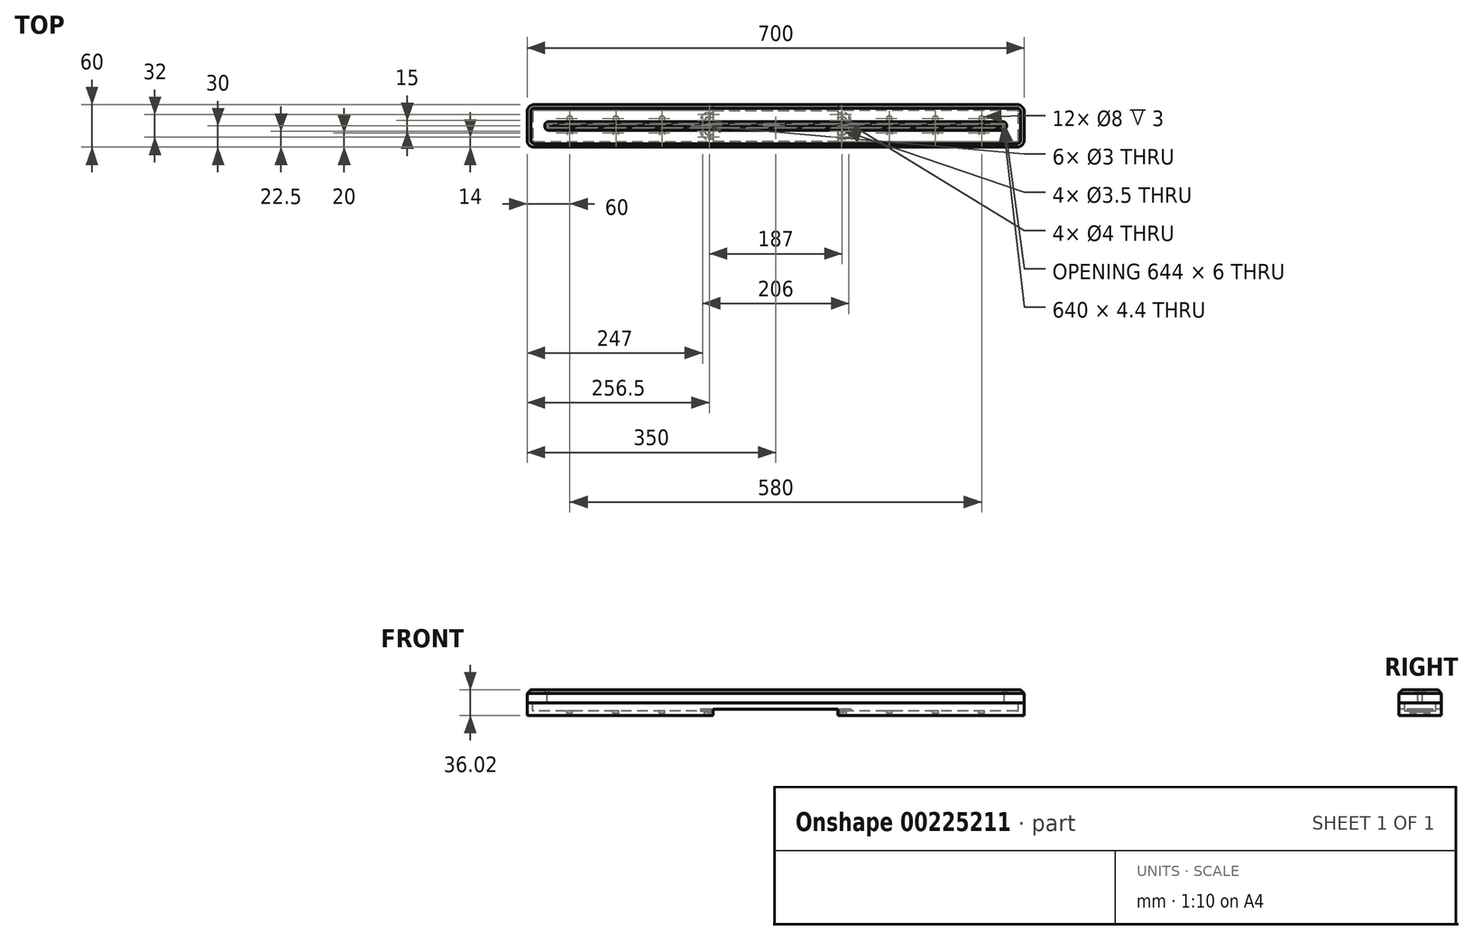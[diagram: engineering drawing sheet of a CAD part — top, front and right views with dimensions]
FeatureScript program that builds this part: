
annotation { "Feature Type Name" : "Feature", "Feature Type Description" : "" }
export const myFeature = defineFeature(function(context is Context, id is Id, definition is map)
    precondition{}
    {
        {
            var Q0;
            Q0=qCreatedBy(makeId("Top.planeOp"),FACE);
            var sketch = newSketch(context, id + "F0", { "sketchPlane" : qUnion([Q0])});
            skLineSegment(sketch, "E0.bottom", {"start": v(350, 30) * mm, "end": v(-350, 30) * mm});
            skLineSegment(sketch, "E0.top", {"start": v(350, -30) * mm, "end": v(-350, -30) * mm});
            skLineSegment(sketch, "E0.left", {"start": v(350, 30) * mm, "end": v(350, -30) * mm});
            skLineSegment(sketch, "E0.right", {"start": v(-350, 30) * mm, "end": v(-350, -30) * mm});
            skPoint(sketch, "E0.middle", {"position": v(0, 0) * mm});
            skSolve(sketch);
        }
        {
            var Q0;
            Q0=makeQuery(id+"F0.imprint","IMPRINT",FACE,{"disambiguationData":[TD([[makeQuery(id+"F0.imprint","IMPRINT",EDGE,{"derivedFrom":sQuery(id+"F0.wireOp",EDGE,"E0.bottom")}),1.0]])]});
            extrude(context, id + "F1", {"entities" : qUnion([Q0]), "depth" : 18 * mm});
        }
        {
            var Q0;
            Q0=makeQuery(id+"F1.opExtrude","CAP_FACE",FACE,{"disambiguationData":[OSD([sQuery(id+"F0.wireOp",EDGE,"E0.bottom"),sQuery(id+"F0.wireOp",EDGE,"E0.top"),sQuery(id+"F0.wireOp",EDGE,"E0.left"),sQuery(id+"F0.wireOp",EDGE,"E0.right")])],"isStart":false});
            extrude(context, id + "F2", {"entities" : qUnion([Q0]), "depth" : 18 * mm});
        }
        {
            var Q0;
            Q0=makeQuery(id+"F1.opExtrude","SWEPT_EDGE",EDGE,{"disambiguationData":[OSD([sQuery(id+"F0.wireOp",EDGE,"E0.top"),sQuery(id+"F0.wireOp",EDGE,"E0.right")])]});
            var Q1;
            Q1=makeQuery(id+"F2.opExtrude","SWEPT_EDGE",EDGE,{"disambiguationData":[OSD([sQuery(id+"F0.wireOp",EDGE,"E0.top"),sQuery(id+"F0.wireOp",EDGE,"E0.right")])]});
            var Q2;
            Q2=makeQuery(id+"F2.opExtrude","SWEPT_EDGE",EDGE,{"disambiguationData":[OSD([sQuery(id+"F0.wireOp",EDGE,"E0.top"),sQuery(id+"F0.wireOp",EDGE,"E0.left")])]});
            var Q3;
            Q3=makeQuery(id+"F1.opExtrude","SWEPT_EDGE",EDGE,{"disambiguationData":[OSD([sQuery(id+"F0.wireOp",EDGE,"E0.top"),sQuery(id+"F0.wireOp",EDGE,"E0.left")])]});
            var Q4;
            Q4=makeQuery(id+"F2.opExtrude","SWEPT_EDGE",EDGE,{"disambiguationData":[OSD([sQuery(id+"F0.wireOp",EDGE,"E0.bottom"),sQuery(id+"F0.wireOp",EDGE,"E0.left")])]});
            var Q5;
            Q5=makeQuery(id+"F1.opExtrude","SWEPT_EDGE",EDGE,{"disambiguationData":[OSD([sQuery(id+"F0.wireOp",EDGE,"E0.bottom"),sQuery(id+"F0.wireOp",EDGE,"E0.left")])]});
            var Q6;
            Q6=makeQuery(id+"F2.opExtrude","SWEPT_EDGE",EDGE,{"disambiguationData":[OSD([sQuery(id+"F0.wireOp",EDGE,"E0.bottom"),sQuery(id+"F0.wireOp",EDGE,"E0.right")])]});
            var Q7;
            Q7=makeQuery(id+"F1.opExtrude","SWEPT_EDGE",EDGE,{"disambiguationData":[OSD([sQuery(id+"F0.wireOp",EDGE,"E0.bottom"),sQuery(id+"F0.wireOp",EDGE,"E0.right")])]});
            fillet(context, id + "F3", {"entities" : qUnion([Q0, Q1, Q2, Q3, Q4, Q5, Q6, Q7]), "radius" : 10 * mm, "tangentPropagation" : true, "allowEdgeOverflow" : false});
        }
        {
            var Q0;
            Q0=makeQuery(id+"F2.opExtrude","CAP_EDGE",EDGE,{"disambiguationData":[OSD([sQuery(id+"F0.wireOp",EDGE,"E0.bottom")])],"isStart":false});
            chamfer(context, id + "F4", {"entities" : qUnion([Q0]), "width" : 5 * mm, "tangentPropagation" : true});
        }
        {
            var Q0;
            Q0=makeQuery(id+"F2.opExtrude","CAP_FACE",FACE,{"disambiguationData":[OSD([sQuery(id+"F0.wireOp",EDGE,"E0.bottom"),sQuery(id+"F0.wireOp",EDGE,"E0.top"),sQuery(id+"F0.wireOp",EDGE,"E0.left"),sQuery(id+"F0.wireOp",EDGE,"E0.right")])],"isStart":false});
            var sketch = newSketch(context, id + "F5", { "sketchPlane" : qUnion([Q0])});
            skLineSegment(sketch, "E1.bottom", {"start": v(-325, 6) * mm, "end": v(325, 6) * mm});
            skLineSegment(sketch, "E1.top", {"start": v(-325, -6) * mm, "end": v(325, -6) * mm});
            skLineSegment(sketch, "E1.left", {"start": v(-325, 6) * mm, "end": v(-325, -6) * mm});
            skLineSegment(sketch, "E1.right", {"start": v(325, 6) * mm, "end": v(325, -6) * mm});
            skPoint(sketch, "E1.middle", {"position": v(0, 0) * mm});
            skSolve(sketch);
        }
        {
            var Q0;
            Q0=makeQuery(id+"F5.imprint","IMPRINT",FACE,{"disambiguationData":[TD([[makeQuery(id+"F5.imprint","IMPRINT",EDGE,{"derivedFrom":sQuery(id+"F5.wireOp",EDGE,"E1.bottom")}),-1.0]])]});
            extrude(context, id + "F6", {"entities" : qUnion([Q0]), "operationType" : NewBodyOperationType.REMOVE, "oppositeDirection" : true, "depth" : 4.4 * mm});
        }
        {
            var Q0;
            Q0=makeQuery(id+"F6.boolean.opBoolean","COPY",EDGE,{"derivedFrom":makeQuery(id+"F6.opExtrude","SWEPT_EDGE",EDGE,{"disambiguationData":[OSD([sQuery(id+"F5.wireOp",EDGE,"E1.bottom"),sQuery(id+"F5.wireOp",EDGE,"E1.left")])]})});
            var Q1;
            Q1=makeQuery(id+"F6.boolean.opBoolean","COPY",EDGE,{"derivedFrom":makeQuery(id+"F6.opExtrude","SWEPT_EDGE",EDGE,{"disambiguationData":[OSD([sQuery(id+"F5.wireOp",EDGE,"E1.top"),sQuery(id+"F5.wireOp",EDGE,"E1.left")])]})});
            var Q2;
            Q2=makeQuery(id+"F6.boolean.opBoolean","COPY",EDGE,{"derivedFrom":makeQuery(id+"F6.opExtrude","SWEPT_EDGE",EDGE,{"disambiguationData":[OSD([sQuery(id+"F5.wireOp",EDGE,"E1.bottom"),sQuery(id+"F5.wireOp",EDGE,"E1.right")])]})});
            var Q3;
            Q3=makeQuery(id+"F6.boolean.opBoolean","COPY",EDGE,{"derivedFrom":makeQuery(id+"F6.opExtrude","SWEPT_EDGE",EDGE,{"disambiguationData":[OSD([sQuery(id+"F5.wireOp",EDGE,"E1.top"),sQuery(id+"F5.wireOp",EDGE,"E1.right")])]})});
            fillet(context, id + "F7", {"entities" : qUnion([Q0, Q1, Q2, Q3]), "radius" : 5 * mm, "tangentPropagation" : true, "allowEdgeOverflow" : false});
        }
        {
            var Q0;
            Q0=makeQuery(id+"F6.boolean.opBoolean","COPY",FACE,{"derivedFrom":makeQuery(id+"F6.opExtrude","CAP_FACE",FACE,{"disambiguationData":[OSD([sQuery(id+"F5.wireOp",EDGE,"E1.bottom"),sQuery(id+"F5.wireOp",EDGE,"E1.top"),sQuery(id+"F5.wireOp",EDGE,"E1.left"),sQuery(id+"F5.wireOp",EDGE,"E1.right")])],"isStart":false})});
            var sketch = newSketch(context, id + "F8", { "sketchPlane" : qUnion([Q0])});
            skArc(sketch, "E2.0", {"start": v(-320, 3) * mm, "mid": v(-321.41, 2.41) * mm, "end": v(-322, 1) * mm});
            skLineSegment(sketch, "E2.1", {"start": v(320, 3) * mm, "end": v(-320, 3) * mm});
            skLineSegment(sketch, "E2.2", {"start": v(-322, 1) * mm, "end": v(-322, -1) * mm});
            skArc(sketch, "E2.3", {"start": v(322, 1) * mm, "mid": v(321.41, 2.41) * mm, "end": v(320, 3) * mm});
            skArc(sketch, "E2.4", {"start": v(-322, -1) * mm, "mid": v(-321.41, -2.41) * mm, "end": v(-320, -3) * mm});
            skLineSegment(sketch, "E2.5", {"start": v(-320, -3) * mm, "end": v(320, -3) * mm});
            skArc(sketch, "E2.6", {"start": v(320, -3) * mm, "mid": v(321.41, -2.41) * mm, "end": v(322, -1) * mm});
            skLineSegment(sketch, "E2.7", {"start": v(322, -1) * mm, "end": v(322, 1) * mm});
            skSolve(sketch);
        }
        {
            var Q0;
            Q0=makeQuery(id+"F8.imprint","IMPRINT",FACE,{"disambiguationData":[TD([[makeQuery(id+"F8.imprint","IMPRINT",EDGE,{"derivedFrom":sQuery(id+"F8.wireOp",EDGE,"E2.0")}),1.0]])]});
            extrude(context, id + "F9", {"entities" : qUnion([Q0]), "operationType" : NewBodyOperationType.REMOVE, "oppositeDirection" : true, "depth" : 25 * mm});
        }
        {
            var Q0;
            Q0=makeQuery(id+"F1.opExtrude","CAP_FACE",FACE,{"disambiguationData":[OSD([sQuery(id+"F0.wireOp",EDGE,"E0.bottom"),sQuery(id+"F0.wireOp",EDGE,"E0.top"),sQuery(id+"F0.wireOp",EDGE,"E0.left"),sQuery(id+"F0.wireOp",EDGE,"E0.right")])],"isStart":false});
            var sketch = newSketch(context, id + "F10", { "sketchPlane" : qUnion([Q0])});
            skArc(sketch, "E3.0", {"start": v(-342, -20) * mm, "mid": v(-341.41, -21.41) * mm, "end": v(-340, -22) * mm});
            skLineSegment(sketch, "E3.1", {"start": v(-342, 20) * mm, "end": v(-342, -20) * mm});
            skLineSegment(sketch, "E3.2", {"start": v(-340, -22) * mm, "end": v(340, -22) * mm});
            skArc(sketch, "E3.3", {"start": v(-340, 22) * mm, "mid": v(-341.41, 21.41) * mm, "end": v(-342, 20) * mm});
            skArc(sketch, "E3.4", {"start": v(340, -22) * mm, "mid": v(341.41, -21.41) * mm, "end": v(342, -20) * mm});
            skLineSegment(sketch, "E3.5", {"start": v(342, -20) * mm, "end": v(342, 20) * mm});
            skArc(sketch, "E3.6", {"start": v(342, 20) * mm, "mid": v(341.41, 21.41) * mm, "end": v(340, 22) * mm});
            skLineSegment(sketch, "E3.7", {"start": v(340, 22) * mm, "end": v(-340, 22) * mm});
            skSolve(sketch);
        }
        {
            var Q0;
            Q0 = qSketchRegion(id + "F10", true);
            extrude(context, id + "F11", {"entities" : qUnion([Q0]), "operationType" : NewBodyOperationType.REMOVE, "oppositeDirection" : true, "depth" : (18 - 6) * mm});
        }
        {
            var Q0;
            Q0=makeQuery(id+"F11.boolean.opBoolean","COPY",FACE,{"derivedFrom":makeQuery(id+"F11.opExtrude","CAP_FACE",FACE,{"disambiguationData":[OSD([sQuery(id+"F10.wireOp",EDGE,"E3.0"),sQuery(id+"F10.wireOp",EDGE,"E3.1"),sQuery(id+"F10.wireOp",EDGE,"E3.2"),sQuery(id+"F10.wireOp",EDGE,"E3.3"),sQuery(id+"F10.wireOp",EDGE,"E3.4"),sQuery(id+"F10.wireOp",EDGE,"E3.5"),sQuery(id+"F10.wireOp",EDGE,"E3.6"),sQuery(id+"F10.wireOp",EDGE,"E3.7")])],"isStart":false})});
            var sketch = newSketch(context, id + "F12", { "sketchPlane" : qUnion([Q0])});
            skLineSegment(sketch, "E4.bottom", {"start": v(-100, 12.5) * mm, "end": v(100, 12.5) * mm});
            skLineSegment(sketch, "E4.top", {"start": v(-100, -12.5) * mm, "end": v(100, -12.5) * mm});
            skLineSegment(sketch, "E4.left", {"start": v(-100, 12.5) * mm, "end": v(-100, -12.5) * mm});
            skLineSegment(sketch, "E4.right", {"start": v(100, 12.5) * mm, "end": v(100, -12.5) * mm});
            skPoint(sketch, "E4.middle", {"position": v(0, 0) * mm});
            skSolve(sketch);
        }
        {
            var Q0;
            Q0=makeQuery(id+"F12.imprint","IMPRINT",FACE,{"disambiguationData":[TD([[makeQuery(id+"F12.imprint","IMPRINT",EDGE,{"derivedFrom":sQuery(id+"F12.wireOp",EDGE,"E4.bottom")}),-1.0]])]});
            extrude(context, id + "F13", {"entities" : qUnion([Q0]), "operationType" : NewBodyOperationType.REMOVE, "oppositeDirection" : true, "depth" : 25 * mm});
        }
        {
            var Q0;
            Q0=makeQuery(id+"F13.boolean.opBoolean","COPY",EDGE,{"derivedFrom":makeQuery(id+"F13.opExtrude","SWEPT_EDGE",EDGE,{"disambiguationData":[OSD([sQuery(id+"F12.wireOp",EDGE,"E4.bottom"),sQuery(id+"F12.wireOp",EDGE,"E4.right")])]})});
            var Q1;
            Q1=makeQuery(id+"F13.boolean.opBoolean","COPY",EDGE,{"derivedFrom":makeQuery(id+"F13.opExtrude","SWEPT_EDGE",EDGE,{"disambiguationData":[OSD([sQuery(id+"F12.wireOp",EDGE,"E4.top"),sQuery(id+"F12.wireOp",EDGE,"E4.right")])]})});
            var Q2;
            Q2=makeQuery(id+"F13.boolean.opBoolean","COPY",EDGE,{"derivedFrom":makeQuery(id+"F13.opExtrude","SWEPT_EDGE",EDGE,{"disambiguationData":[OSD([sQuery(id+"F12.wireOp",EDGE,"E4.top"),sQuery(id+"F12.wireOp",EDGE,"E4.left")])]})});
            var Q3;
            Q3=makeQuery(id+"F13.boolean.opBoolean","COPY",EDGE,{"derivedFrom":makeQuery(id+"F13.opExtrude","SWEPT_EDGE",EDGE,{"disambiguationData":[OSD([sQuery(id+"F12.wireOp",EDGE,"E4.bottom"),sQuery(id+"F12.wireOp",EDGE,"E4.left")])]})});
            fillet(context, id + "F14", {"entities" : qUnion([Q0, Q1, Q2, Q3]), "radius" : 5 * mm, "tangentPropagation" : true, "allowEdgeOverflow" : false});
        }
        {
            var Q0;
            Q0=makeQuery(id+"F11.boolean.opBoolean","COPY",FACE,{"derivedFrom":makeQuery(id+"F11.opExtrude","CAP_FACE",FACE,{"disambiguationData":[OSD([sQuery(id+"F10.wireOp",EDGE,"E3.0"),sQuery(id+"F10.wireOp",EDGE,"E3.1"),sQuery(id+"F10.wireOp",EDGE,"E3.2"),sQuery(id+"F10.wireOp",EDGE,"E3.3"),sQuery(id+"F10.wireOp",EDGE,"E3.4"),sQuery(id+"F10.wireOp",EDGE,"E3.5"),sQuery(id+"F10.wireOp",EDGE,"E3.6"),sQuery(id+"F10.wireOp",EDGE,"E3.7")])],"isStart":false})});
            var sketch = newSketch(context, id + "F15", { "sketchPlane" : qUnion([Q0])});
            skCircle(sketch, "E5", {"center": v(-225, -10) * mm, "radius": 4 * mm});
            skCircle(sketch, "E6", {"center": v(-225, 10) * mm, "radius": 4 * mm});
            skCircle(sketch, "E7", {"center": v(-160, 10) * mm, "radius": 4 * mm});
            skCircle(sketch, "E8", {"center": v(-160, -10) * mm, "radius": 4 * mm});
            skCircle(sketch, "E9", {"center": v(-290, 10) * mm, "radius": 4 * mm});
            skCircle(sketch, "E10", {"center": v(-290, -10) * mm, "radius": 4 * mm});
            skCircle(sketch, "E11.MirrorC", {"center": v(290, -10) * mm, "radius": 4 * mm});
            skCircle(sketch, "E12.MirrorC", {"center": v(160, 10) * mm, "radius": 4 * mm});
            skCircle(sketch, "E13.MirrorC", {"center": v(225, 10) * mm, "radius": 4 * mm});
            skCircle(sketch, "E14.MirrorC", {"center": v(225, -10) * mm, "radius": 4 * mm});
            skCircle(sketch, "E15.MirrorC", {"center": v(290, 10) * mm, "radius": 4 * mm});
            skCircle(sketch, "E16.MirrorC", {"center": v(160, -10) * mm, "radius": 4 * mm});
            skSolve(sketch);
        }
        {
            var Q0;
            Q0 = qSketchRegion(id + "F15", true);
            extrude(context, id + "F16", {"entities" : qUnion([Q0]), "operationType" : NewBodyOperationType.REMOVE, "oppositeDirection" : true, "depth" : 3 * mm});
        }
        {
            var Q0;
            Q0=makeQuery(id+"F6.boolean.opBoolean","COPY",FACE,{"derivedFrom":makeQuery(id+"F6.opExtrude","CAP_FACE",FACE,{"disambiguationData":[OSD([sQuery(id+"F5.wireOp",EDGE,"E1.bottom"),sQuery(id+"F5.wireOp",EDGE,"E1.top"),sQuery(id+"F5.wireOp",EDGE,"E1.left"),sQuery(id+"F5.wireOp",EDGE,"E1.right")])],"isStart":false})});
            var sketch = newSketch(context, id + "F17", { "sketchPlane" : qUnion([Q0])});
            skArc(sketch, "E17.0", {"start": v(-320, 6) * mm, "mid": v(-323.54, 4.54) * mm, "end": v(-325, 1) * mm});
            skLineSegment(sketch, "E17.1", {"start": v(320, 6) * mm, "end": v(-320, 6) * mm});
            skLineSegment(sketch, "E17.2", {"start": v(-325, 1) * mm, "end": v(-325, -1) * mm});
            skArc(sketch, "E17.3", {"start": v(325, 1) * mm, "mid": v(323.54, 4.54) * mm, "end": v(320, 6) * mm});
            skArc(sketch, "E17.4", {"start": v(-325, -1) * mm, "mid": v(-323.54, -4.54) * mm, "end": v(-320, -6) * mm});
            skLineSegment(sketch, "E17.5", {"start": v(-320, -6) * mm, "end": v(320, -6) * mm});
            skArc(sketch, "E17.6", {"start": v(320, -6) * mm, "mid": v(323.54, -4.54) * mm, "end": v(325, -1) * mm});
            skLineSegment(sketch, "E17.7", {"start": v(325, -1) * mm, "end": v(325, 1) * mm});
            skLineSegment(sketch, "E18.bottom", {"start": v(-320, -2.2) * mm, "end": v(320, -2.2) * mm});
            skLineSegment(sketch, "E18.top", {"start": v(-320, 2.2) * mm, "end": v(320, 2.2) * mm});
            skLineSegment(sketch, "E18.left", {"start": v(-320, -2.2) * mm, "end": v(-320, 2.2) * mm});
            skLineSegment(sketch, "E18.right", {"start": v(320, -2.2) * mm, "end": v(320, 2.2) * mm});
            skPoint(sketch, "E18.middle", {"position": v(0, 0) * mm});
            skSolve(sketch);
        }
        {
            var Q0;
            Q0 = qSketchRegion(id + "F17", true);
            extrude(context, id + "F18", {"entities" : qUnion([Q0]), "depth" : 4.42 * mm});
        }
        {
            var Q0;
            Q0=makeQuery(id+"F11.boolean.opBoolean","COPY",FACE,{"derivedFrom":makeQuery(id+"F11.opExtrude","CAP_FACE",FACE,{"disambiguationData":[OSD([sQuery(id+"F10.wireOp",EDGE,"E3.0"),sQuery(id+"F10.wireOp",EDGE,"E3.1"),sQuery(id+"F10.wireOp",EDGE,"E3.2"),sQuery(id+"F10.wireOp",EDGE,"E3.3"),sQuery(id+"F10.wireOp",EDGE,"E3.4"),sQuery(id+"F10.wireOp",EDGE,"E3.5"),sQuery(id+"F10.wireOp",EDGE,"E3.6"),sQuery(id+"F10.wireOp",EDGE,"E3.7")])],"isStart":false})});
            var sketch = newSketch(context, id + "F19", { "sketchPlane" : qUnion([Q0])});
            skArc(sketch, "E19.0", {"start": v(-106, 7.5) * mm, "mid": v(-102.78, 15.28) * mm, "end": v(-95, 18.5) * mm});
            skLineSegment(sketch, "E19.1", {"start": v(-106, 7.5) * mm, "end": v(-106, -7.5) * mm});
            skLineSegment(sketch, "E19.2", {"start": v(-95, 18.5) * mm, "end": v(95, 18.5) * mm});
            skArc(sketch, "E19.3", {"start": v(-95, -18.5) * mm, "mid": v(-102.78, -15.28) * mm, "end": v(-106, -7.5) * mm});
            skArc(sketch, "E19.4", {"start": v(95, 18.5) * mm, "mid": v(102.78, 15.28) * mm, "end": v(106, 7.5) * mm});
            skLineSegment(sketch, "E19.5", {"start": v(106, 7.5) * mm, "end": v(106, -7.5) * mm});
            skArc(sketch, "E19.6", {"start": v(106, -7.5) * mm, "mid": v(102.78, -15.28) * mm, "end": v(95, -18.5) * mm});
            skLineSegment(sketch, "E19.7", {"start": v(-95, -18.5) * mm, "end": v(95, -18.5) * mm});
            skLineSegment(sketch, "E20.2", {"start": v(-86, 10.5) * mm, "end": v(86, 10.5) * mm});
            skLineSegment(sketch, "E20.7", {"start": v(-86, -10.5) * mm, "end": v(86, -10.5) * mm});
            skLineSegment(sketch, "E21", {"start": v(-88, 8.5) * mm, "end": v(-88, -8.5) * mm});
            skLineSegment(sketch, "E22", {"start": v(88, 8.5) * mm, "end": v(88, -8.5) * mm});
            skCircle(sketch, "E23", {"center": v(-103, 0) * mm, "radius": 1.5 * mm});
            skPoint(sketch, "E23.centerSnap0", {"position": v(-106, 0) * mm});
            skCircle(sketch, "E24", {"center": v(-93, 16) * mm, "radius": 1.5 * mm});
            skCircle(sketch, "E25", {"center": v(-25, 16) * mm, "radius": 1.5 * mm});
            skCircle(sketch, "E26", {"center": v(-93.5, -7.5) * mm, "radius": 2 * mm});
            skPoint(sketch, "E27.visualSharp", {"position": v(-88, 10.5) * mm});
            skArc(sketch, "E27.filletArc", {"start": v(-86, 10.5) * mm, "mid": v(-87.41, 9.91) * mm, "end": v(-88, 8.5) * mm});
            skPoint(sketch, "E28.visualSharp", {"position": v(-88, -10.5) * mm});
            skArc(sketch, "E28.filletArc", {"start": v(-88, -8.5) * mm, "mid": v(-87.41, -9.91) * mm, "end": v(-86, -10.5) * mm});
            skPoint(sketch, "E29.visualSharp", {"position": v(88, 10.5) * mm});
            skArc(sketch, "E29.filletArc", {"start": v(88, 8.5) * mm, "mid": v(87.41, 9.91) * mm, "end": v(86, 10.5) * mm});
            skPoint(sketch, "E30.visualSharp", {"position": v(88, -10.5) * mm});
            skArc(sketch, "E30.filletArc", {"start": v(86, -10.5) * mm, "mid": v(87.41, -9.91) * mm, "end": v(88, -8.5) * mm});
            skCircle(sketch, "E31.MirrorC", {"center": v(-93.5, 7.5) * mm, "radius": 2 * mm});
            skCircle(sketch, "E32.MirrorC", {"center": v(-93, -16) * mm, "radius": 1.5 * mm});
            skCircle(sketch, "E33.MirrorC", {"center": v(-25, -16) * mm, "radius": 1.5 * mm});
            skCircle(sketch, "E34.MirrorC", {"center": v(25, 16) * mm, "radius": 1.5 * mm});
            skCircle(sketch, "E35.MirrorC", {"center": v(93, -16) * mm, "radius": 1.5 * mm});
            skCircle(sketch, "E36.MirrorC", {"center": v(93, 16) * mm, "radius": 1.5 * mm});
            skCircle(sketch, "E37.MirrorC", {"center": v(93.5, 7.5) * mm, "radius": 2 * mm});
            skCircle(sketch, "E38.MirrorC", {"center": v(93.5, -7.5) * mm, "radius": 2 * mm});
            skCircle(sketch, "E39.MirrorC", {"center": v(103, 0) * mm, "radius": 1.5 * mm});
            skSolve(sketch);
        }
        {
            var Q0;
            Q0 = qSketchRegion(id + "F19", true);
            extrude(context, id + "F20", {"entities" : qUnion([Q0]), "depth" : 2.5 * mm});
        }
        {
            var Q0;
            Q0=makeQuery(id+"F20.opExtrude","CAP_FACE",FACE,{"disambiguationData":[OSD([sQuery(id+"F19.wireOp",EDGE,"E19.0"),sQuery(id+"F19.wireOp",EDGE,"E19.1"),sQuery(id+"F19.wireOp",EDGE,"E19.2"),sQuery(id+"F19.wireOp",EDGE,"E19.3"),sQuery(id+"F19.wireOp",EDGE,"E19.4"),sQuery(id+"F19.wireOp",EDGE,"E19.5"),sQuery(id+"F19.wireOp",EDGE,"E19.6"),sQuery(id+"F19.wireOp",EDGE,"E19.7"),sQuery(id+"F19.wireOp",EDGE,"E20.2"),sQuery(id+"F19.wireOp",EDGE,"E20.7"),sQuery(id+"F19.wireOp",EDGE,"E21"),sQuery(id+"F19.wireOp",EDGE,"E22"),sQuery(id+"F19.wireOp",EDGE,"E23"),sQuery(id+"F19.wireOp",EDGE,"E24"),sQuery(id+"F19.wireOp",EDGE,"E25"),sQuery(id+"F19.wireOp",EDGE,"E26"),sQuery(id+"F19.wireOp",EDGE,"E27.filletArc"),sQuery(id+"F19.wireOp",EDGE,"E28.filletArc"),sQuery(id+"F19.wireOp",EDGE,"E29.filletArc"),sQuery(id+"F19.wireOp",EDGE,"E30.filletArc"),sQuery(id+"F19.wireOp",EDGE,"E31.MirrorC"),sQuery(id+"F19.wireOp",EDGE,"E32.MirrorC"),sQuery(id+"F19.wireOp",EDGE,"E33.MirrorC"),sQuery(id+"F19.wireOp",EDGE,"E34.MirrorC"),sQuery(id+"F19.wireOp",EDGE,"E35.MirrorC"),sQuery(id+"F19.wireOp",EDGE,"E36.MirrorC"),sQuery(id+"F19.wireOp",EDGE,"E37.MirrorC"),sQuery(id+"F19.wireOp",EDGE,"E38.MirrorC"),sQuery(id+"F19.wireOp",EDGE,"E39.MirrorC")])],"isStart":true});
            var sketch = newSketch(context, id + "F21", { "sketchPlane" : qUnion([Q0])});
            skLineSegment(sketch, "E40.0", {"start": v(-99.5, -7.5) * mm, "end": v(-99.5, 7.5) * mm});
            skArc(sketch, "E40.1", {"start": v(-95, -12) * mm, "mid": v(-98.18, -10.68) * mm, "end": v(-99.5, -7.5) * mm});
            skArc(sketch, "E40.2", {"start": v(-99.5, 7.5) * mm, "mid": v(-98.18, 10.68) * mm, "end": v(-95, 12) * mm});
            skLineSegment(sketch, "E40.3", {"start": v(-95, -12) * mm, "end": v(95, -12) * mm});
            skLineSegment(sketch, "E40.4", {"start": v(-95, 12) * mm, "end": v(95, 12) * mm});
            skArc(sketch, "E40.5", {"start": v(95, 12) * mm, "mid": v(98.18, 10.68) * mm, "end": v(99.5, 7.5) * mm});
            skLineSegment(sketch, "E40.6", {"start": v(99.5, -7.5) * mm, "end": v(99.5, 7.5) * mm});
            skArc(sketch, "E40.7", {"start": v(99.5, -7.5) * mm, "mid": v(98.18, -10.68) * mm, "end": v(95, -12) * mm});
            skCircle(sketch, "E41", {"center": v(-93.5, 7.5) * mm, "radius": 2 * mm});
            skCircle(sketch, "E42", {"center": v(-93.5, -7.5) * mm, "radius": 2 * mm});
            skCircle(sketch, "E43.MirrorC", {"center": v(93.5, 7.5) * mm, "radius": 2 * mm});
            skCircle(sketch, "E44.MirrorC", {"center": v(93.5, -7.5) * mm, "radius": 2 * mm});
            skArc(sketch, "E45.0", {"start": v(-88, 8.5) * mm, "mid": v(-87.41, 9.91) * mm, "end": v(-86, 10.5) * mm});
            skLineSegment(sketch, "E45.1", {"start": v(-88, -8.5) * mm, "end": v(-88, 8.5) * mm});
            skLineSegment(sketch, "E45.2", {"start": v(-86, 10.5) * mm, "end": v(86, 10.5) * mm});
            skArc(sketch, "E45.3", {"start": v(-86, -10.5) * mm, "mid": v(-87.41, -9.91) * mm, "end": v(-88, -8.5) * mm});
            skArc(sketch, "E45.4", {"start": v(86, 10.5) * mm, "mid": v(87.41, 9.91) * mm, "end": v(88, 8.5) * mm});
            skLineSegment(sketch, "E45.5", {"start": v(88, -8.5) * mm, "end": v(88, 8.5) * mm});
            skArc(sketch, "E45.6", {"start": v(88, -8.5) * mm, "mid": v(87.41, -9.91) * mm, "end": v(86, -10.5) * mm});
            skLineSegment(sketch, "E45.7", {"start": v(-86, -10.5) * mm, "end": v(86, -10.5) * mm});
            skSolve(sketch);
        }
        {
            var Q0;
            Q0 = qSketchRegion(id + "F21", true);
            extrude(context, id + "F22", {"entities" : qUnion([Q0]), "operationType" : NewBodyOperationType.ADD, "depth" : 1 * mm});
        }
        {
            var Q0;
            Q0=makeQuery(id+"F22.opExtrude","CAP_FACE",FACE,{"disambiguationData":[OSD([sQuery(id+"F21.wireOp",EDGE,"E40.0"),sQuery(id+"F21.wireOp",EDGE,"E40.1"),sQuery(id+"F21.wireOp",EDGE,"E40.2"),sQuery(id+"F21.wireOp",EDGE,"E40.3"),sQuery(id+"F21.wireOp",EDGE,"E40.4"),sQuery(id+"F21.wireOp",EDGE,"E40.5"),sQuery(id+"F21.wireOp",EDGE,"E40.6"),sQuery(id+"F21.wireOp",EDGE,"E40.7"),sQuery(id+"F21.wireOp",EDGE,"E41"),sQuery(id+"F21.wireOp",EDGE,"E42"),sQuery(id+"F21.wireOp",EDGE,"E43.MirrorC"),sQuery(id+"F21.wireOp",EDGE,"E44.MirrorC"),sQuery(id+"F21.wireOp",EDGE,"E45.0"),sQuery(id+"F21.wireOp",EDGE,"E45.1"),sQuery(id+"F21.wireOp",EDGE,"E45.2"),sQuery(id+"F21.wireOp",EDGE,"E45.3"),sQuery(id+"F21.wireOp",EDGE,"E45.4"),sQuery(id+"F21.wireOp",EDGE,"E45.5"),sQuery(id+"F21.wireOp",EDGE,"E45.6"),sQuery(id+"F21.wireOp",EDGE,"E45.7")])],"isStart":false});
            var sketch = newSketch(context, id + "F23", { "sketchPlane" : qUnion([Q0])});
            skArc(sketch, "E46.0", {"start": v(-99.5, 7.5) * mm, "mid": v(-98.18, 10.68) * mm, "end": v(-95, 12) * mm});
            skLineSegment(sketch, "E46.1", {"start": v(-99.5, -7.5) * mm, "end": v(-99.5, 7.5) * mm});
            skLineSegment(sketch, "E46.2", {"start": v(-95, 12) * mm, "end": v(95, 12) * mm});
            skArc(sketch, "E46.3", {"start": v(-95, -12) * mm, "mid": v(-98.18, -10.68) * mm, "end": v(-99.5, -7.5) * mm});
            skArc(sketch, "E46.4", {"start": v(95, 12) * mm, "mid": v(98.18, 10.68) * mm, "end": v(99.5, 7.5) * mm});
            skLineSegment(sketch, "E46.5", {"start": v(99.5, -7.5) * mm, "end": v(99.5, 7.5) * mm});
            skArc(sketch, "E46.6", {"start": v(99.5, -7.5) * mm, "mid": v(98.18, -10.68) * mm, "end": v(95, -12) * mm});
            skLineSegment(sketch, "E46.7", {"start": v(-95, -12) * mm, "end": v(95, -12) * mm});
            skCircle(sketch, "E47", {"center": v(93.5, 7.5) * mm, "radius": 1.75 * mm});
            skCircle(sketch, "E48", {"center": v(93.5, -7.5) * mm, "radius": 1.75 * mm});
            skCircle(sketch, "E49", {"center": v(-93.5, 7.5) * mm, "radius": 1.75 * mm});
            skCircle(sketch, "E50", {"center": v(-93.5, -7.5) * mm, "radius": 1.75 * mm});
            skSolve(sketch);
        }
        {
            var Q0;
            Q0 = qSketchRegion(id + "F23", true);
            extrude(context, id + "F24", {"entities" : qUnion([Q0]), "depth" : 5 * mm});
        }
        {
            var Q0;
            Q0=makeQuery(id+"F20.opExtrude","CAP_FACE",FACE,{"disambiguationData":[OSD([sQuery(id+"F19.wireOp",EDGE,"E19.0"),sQuery(id+"F19.wireOp",EDGE,"E19.1"),sQuery(id+"F19.wireOp",EDGE,"E19.2"),sQuery(id+"F19.wireOp",EDGE,"E19.3"),sQuery(id+"F19.wireOp",EDGE,"E19.4"),sQuery(id+"F19.wireOp",EDGE,"E19.5"),sQuery(id+"F19.wireOp",EDGE,"E19.6"),sQuery(id+"F19.wireOp",EDGE,"E19.7"),sQuery(id+"F19.wireOp",EDGE,"E20.2"),sQuery(id+"F19.wireOp",EDGE,"E20.7"),sQuery(id+"F19.wireOp",EDGE,"E21"),sQuery(id+"F19.wireOp",EDGE,"E22"),sQuery(id+"F19.wireOp",EDGE,"E23"),sQuery(id+"F19.wireOp",EDGE,"E24"),sQuery(id+"F19.wireOp",EDGE,"E25"),sQuery(id+"F19.wireOp",EDGE,"E26"),sQuery(id+"F19.wireOp",EDGE,"E27.filletArc"),sQuery(id+"F19.wireOp",EDGE,"E28.filletArc"),sQuery(id+"F19.wireOp",EDGE,"E29.filletArc"),sQuery(id+"F19.wireOp",EDGE,"E30.filletArc"),sQuery(id+"F19.wireOp",EDGE,"E31.MirrorC"),sQuery(id+"F19.wireOp",EDGE,"E32.MirrorC"),sQuery(id+"F19.wireOp",EDGE,"E33.MirrorC"),sQuery(id+"F19.wireOp",EDGE,"E34.MirrorC"),sQuery(id+"F19.wireOp",EDGE,"E35.MirrorC"),sQuery(id+"F19.wireOp",EDGE,"E36.MirrorC"),sQuery(id+"F19.wireOp",EDGE,"E37.MirrorC"),sQuery(id+"F19.wireOp",EDGE,"E38.MirrorC"),sQuery(id+"F19.wireOp",EDGE,"E39.MirrorC")])],"isStart":false});
            var sketch = newSketch(context, id + "F25", { "sketchPlane" : qUnion([Q0])});
            skLineSegment(sketch, "E51.bottom", {"start": v(-88, 42.32) * mm, "end": v(88, 42.32) * mm});
            skLineSegment(sketch, "E51.top", {"start": v(-88, -42.32) * mm, "end": v(88, -42.32) * mm});
            skLineSegment(sketch, "E51.left", {"start": v(-88, 42.32) * mm, "end": v(-88, -42.32) * mm});
            skLineSegment(sketch, "E51.right", {"start": v(88, 42.32) * mm, "end": v(88, -42.32) * mm});
            skPoint(sketch, "E51.middle", {"position": v(0, 0) * mm});
            skSolve(sketch);
        }
        {
            var Q0;
            Q0 = qSketchRegion(id + "F25", true);
            extrude(context, id + "F26", {"entities" : qUnion([Q0]), "operationType" : NewBodyOperationType.REMOVE, "oppositeDirection" : true, "depth" : 25 * mm});
        }
        {
            var Q0;
            Q0=makeQuery(id+"F26.boolean.opBoolean","INTERSECT",EDGE,{"derivedFrom":[makeQuery(id+"F20.opExtrude","SWEPT_FACE",FACE,{"disambiguationData":[OSD([sQuery(id+"F19.wireOp",EDGE,"E19.2")])]}),makeQuery(id+"F26.opExtrude","SWEPT_FACE",FACE,{"disambiguationData":[OSD([sQuery(id+"F25.wireOp",EDGE,"E51.left")])]})]});
            var Q1;
            Q1=makeQuery(id+"F26.boolean.opBoolean","INTERSECT",EDGE,{"derivedFrom":[makeQuery(id+"F20.opExtrude","SWEPT_FACE",FACE,{"disambiguationData":[OSD([sQuery(id+"F19.wireOp",EDGE,"E19.7")])]}),makeQuery(id+"F26.opExtrude","SWEPT_FACE",FACE,{"disambiguationData":[OSD([sQuery(id+"F25.wireOp",EDGE,"E51.left")])]})]});
            fillet(context, id + "F27", {"entities" : qUnion([Q0, Q1]), "radius" : 2 * mm, "tangentPropagation" : true, "allowEdgeOverflow" : false});
        }
    });
